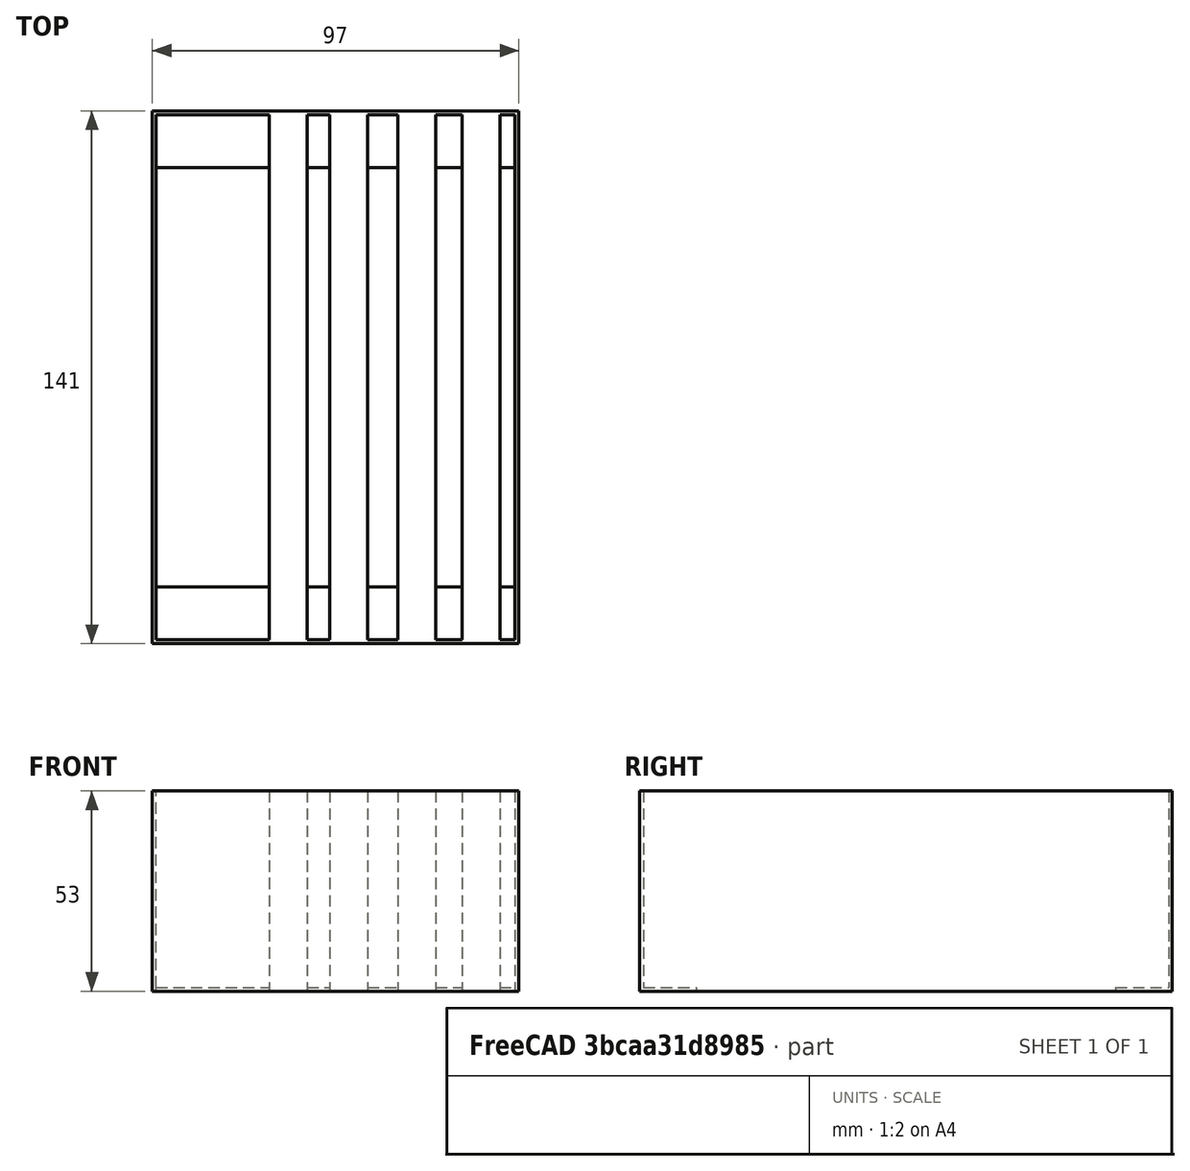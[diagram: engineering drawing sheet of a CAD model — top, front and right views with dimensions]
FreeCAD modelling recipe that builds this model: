
FCSTD DOCUMENT  (FreeCAD 0.18R4 (GitTag))
Label: characters
License: All rights reserved
LicenseURL: http://en.wikipedia.org/wiki/All_rights_reserved
objects: Part::Box×10, Part::Cut×2, Part::MultiFuse×2
note: 14 computed .brp shape members not serialized (recipe doc carries the construction recipe); baked Part::Feature solids carry a one-line shape summary decoded from their .brp

FEATURE [Part::Box] Box  label="Cube"
  AttacherType = Attacher::AttachEngine3D
  Height = 53
  Length = 307
  Placement = pos=(1,1,0) rot=(0,0,1;0rad)
  Width = 139
FEATURE [Part::Box] Box001  label="Cube001"
  AttacherType = Attacher::AttachEngine3D
  Height = 53
  Length = 309
  Width = 141
FEATURE [Part::Cut] Cut
  Base = -> Box001
  Tool = -> Box
FEATURE [Part::Box] Box002  label="Cube002"
  AttacherType = Attacher::AttachEngine3D
  Height = 1
  Length = 309
  Width = 15
FEATURE [Part::Box] Box003  label="Cube003"
  AttacherType = Attacher::AttachEngine3D
  Height = 1
  Length = 309
  Placement = pos=(0,126,0) rot=(0,0,1;0rad)
  Width = 15
FEATURE [Part::MultiFuse] Fusion
  Shapes = -> [Cut,Box002,Box003]
FEATURE [Part::Box] Box004  label="Cube004"
  AttacherType = Attacher::AttachEngine3D
  Height = 53
  Length = 10
  Placement = pos=(31,0,0) rot=(0,0,1;0rad)
  Width = 141
FEATURE [Part::Box] Box005  label="Cube005"
  AttacherType = Attacher::AttachEngine3D
  Height = 53
  Length = 10
  Placement = pos=(47,0,0) rot=(0,0,1;0rad)
  Width = 141
FEATURE [Part::Box] Box006  label="Cube006"
  AttacherType = Attacher::AttachEngine3D
  Height = 53
  Length = 10
  Placement = pos=(65,0,0) rot=(0,0,1;0rad)
  Width = 141
FEATURE [Part::Box] Box007  label="Cube007"
  AttacherType = Attacher::AttachEngine3D
  Height = 53
  Length = 10
  Placement = pos=(82,0,0) rot=(0,0,1;0rad)
  Width = 141
FEATURE [Part::Box] Box008  label="Cube008"
  AttacherType = Attacher::AttachEngine3D
  Height = 53
  Length = 10
  Placement = pos=(96,0,0) rot=(0,0,1;0rad)
  Width = 141
FEATURE [Part::Box] Box009  label="Cube009"
  AttacherType = Attacher::AttachEngine3D
  Height = 53
  Length = 212
  Placement = pos=(97,0,0) rot=(0,0,1;0rad)
  Width = 141
FEATURE [Part::MultiFuse] Fusion001
  Shapes = -> [Fusion,Box008,Box005,Box007,Box006,Box004]
FEATURE [Part::Cut] Cut001
  Base = -> Fusion001
  Tool = -> Box009
